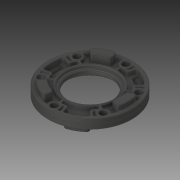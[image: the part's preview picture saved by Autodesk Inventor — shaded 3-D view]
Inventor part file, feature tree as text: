
AUTODESK INVENTOR PART (.ipt)
format: ipt  version: 2019 (Build 230136000, 136)  size: 1,747,456 bytes
history: native  units: in
note: dims shown in document units (in); Inventor stores cm internally (conversion verified against a paired STEP export)
features: fillet x1
ambient origin geometry x8: Origin, YZ Plane, XZ Plane, XY Plane, X Axis, Y Axis, Z Axis, Center Point
bodies: Solid1 (feature_tree)
feature tree (1):
  fillet  "Fillet10"  [1 undecoded]
note: 1 required parameter value undecoded (feature->parameter linkage not recoverable at this tier; creation-order binding heuristic only, values carry confidence <= 0.55)
